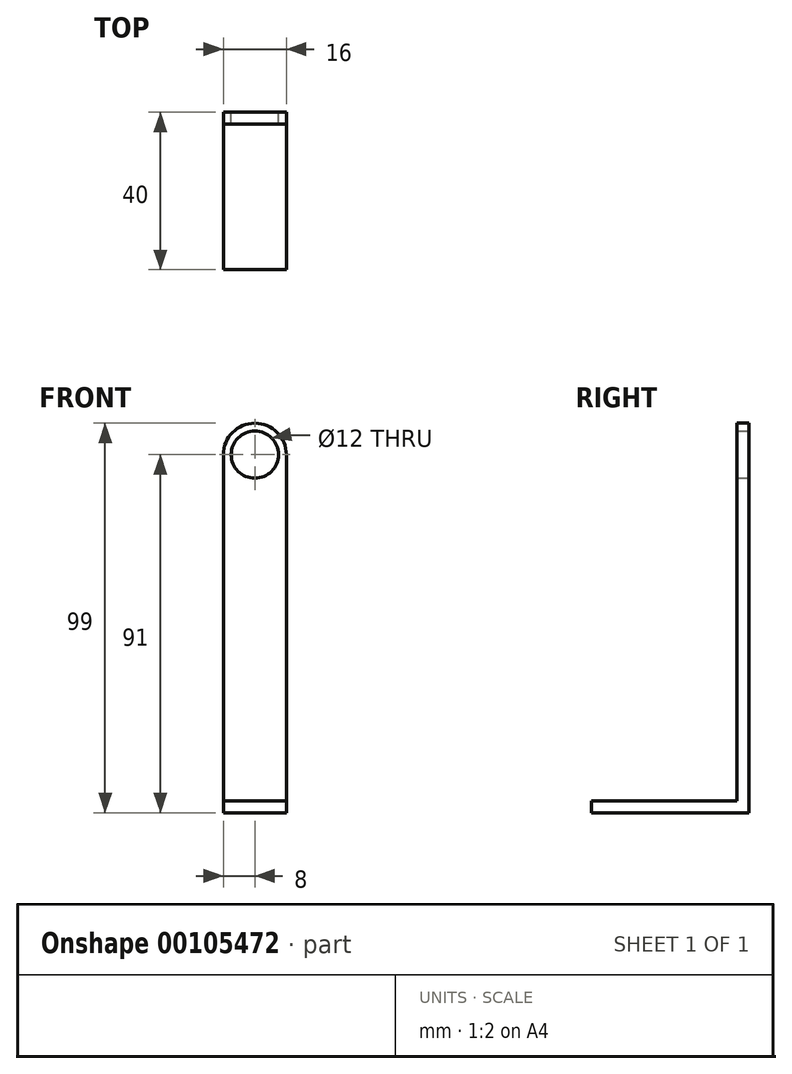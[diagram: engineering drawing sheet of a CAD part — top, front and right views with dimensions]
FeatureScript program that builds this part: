
annotation { "Feature Type Name" : "Feature", "Feature Type Description" : "" }
export const myFeature = defineFeature(function(context is Context, id is Id, definition is map)
    precondition{}
    {
        {
            var Q0;
            Q0=qCreatedBy(makeId("Front.planeOp"),FACE);
            var sketch = newSketch(context, id + "F0", { "sketchPlane" : qUnion([Q0])});
            skCircle(sketch, "E0", {"center": v(0, 0) * mm, "radius": 6 * mm});
            skLineSegment(sketch, "E1.top", {"start": v(-8, -91) * mm, "end": v(8, -91) * mm});
            skLineSegment(sketch, "E1.left", {"start": v(-8, 0) * mm, "end": v(-8, -91) * mm});
            skLineSegment(sketch, "E1.right", {"start": v(8, 0) * mm, "end": v(8, -91) * mm});
            skArc(sketch, "E2", {"start": v(8, 0) * mm, "mid": v(0, 8) * mm, "end": v(-8, 0) * mm});
            skSolve(sketch);
        }
        {
            var Q0;
            Q0 = qSketchRegion(id + "F0", true);
            extrude(context, id + "F1", {"entities" : qUnion([Q0]), "depth" : 3 * mm});
        }
        {
            var Q0;
            Q0=qCreatedBy(makeId("Front.planeOp"),FACE);
            var sketch = newSketch(context, id + "F2", { "sketchPlane" : qUnion([Q0])});
            skLineSegment(sketch, "E3.bottom", {"start": v(-8, -91) * mm, "end": v(8, -91) * mm});
            skLineSegment(sketch, "E3.top", {"start": v(-8, -88) * mm, "end": v(8, -88) * mm});
            skLineSegment(sketch, "E3.left", {"start": v(-8, -91) * mm, "end": v(-8, -88) * mm});
            skLineSegment(sketch, "E3.right", {"start": v(8, -91) * mm, "end": v(8, -88) * mm});
            skSolve(sketch);
        }
        {
            var Q0;
            Q0 = qSketchRegion(id + "F2", true);
            extrude(context, id + "F3", {"entities" : qUnion([Q0]), "operationType" : NewBodyOperationType.ADD, "depth" : 40 * mm});
        }
    });
